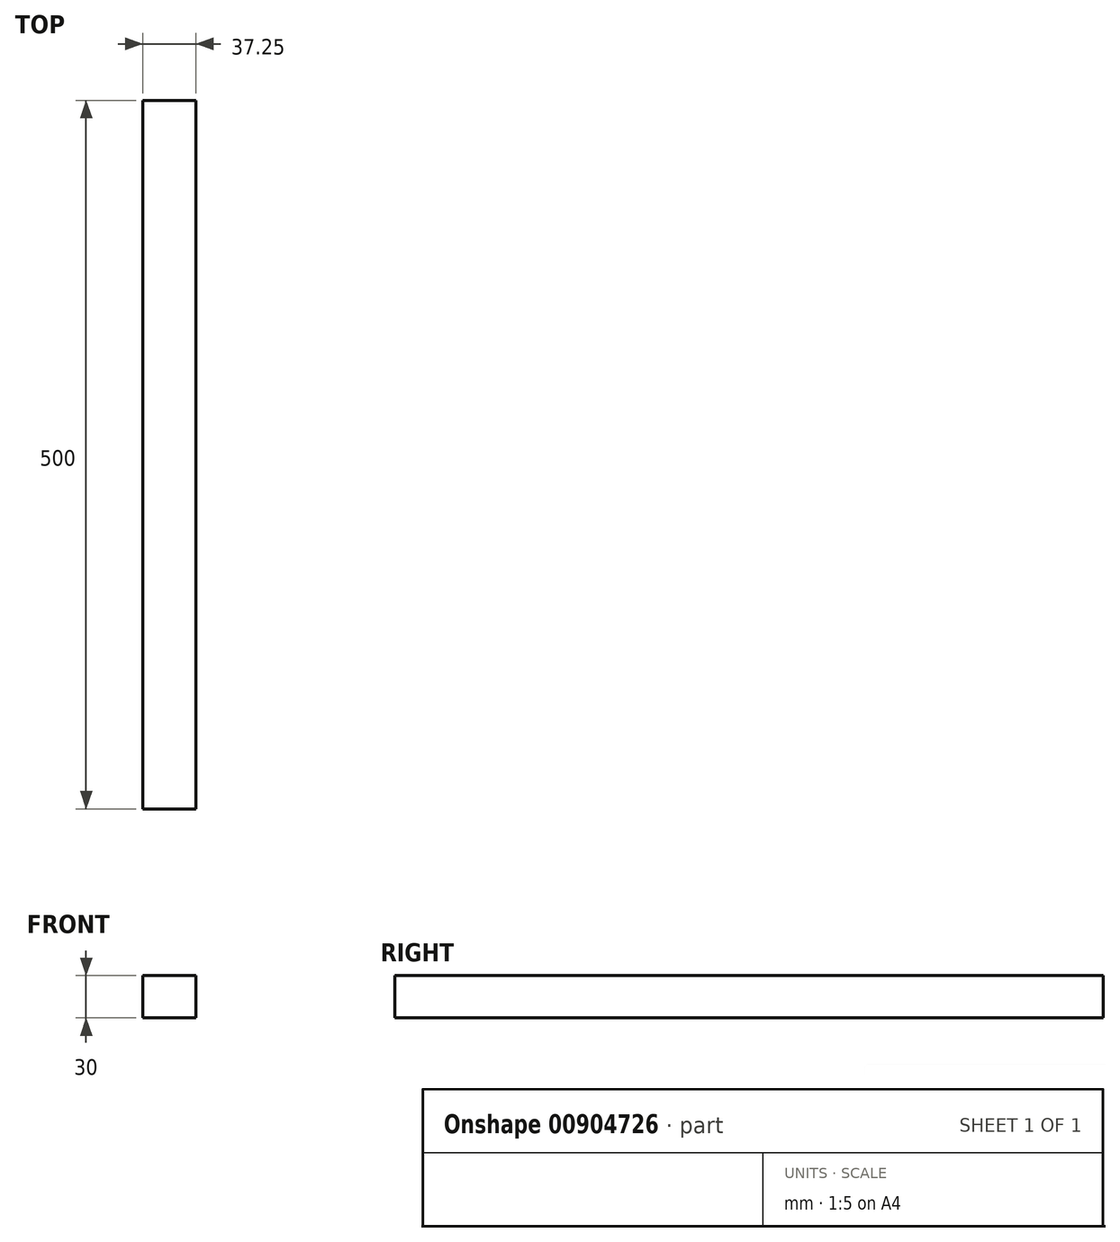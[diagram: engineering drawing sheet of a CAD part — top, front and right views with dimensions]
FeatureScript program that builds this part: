
annotation { "Feature Type Name" : "Feature", "Feature Type Description" : "" }
export const myFeature = defineFeature(function(context is Context, id is Id, definition is map)
    precondition{}
    {
        {
            var Q0;
            Q0=qCreatedBy(makeId("Front.planeOp"),FACE);
            var sketch = newSketch(context, id + "F0", { "sketchPlane" : qUnion([Q0])});
            skLineSegment(sketch, "E0.bottom", {"start": v(0, 0) * mm, "end": v(37.25, 0) * mm});
            skLineSegment(sketch, "E0.top", {"start": v(0, 30) * mm, "end": v(37.25, 30) * mm});
            skLineSegment(sketch, "E0.left", {"start": v(0, 0) * mm, "end": v(0, 30) * mm});
            skLineSegment(sketch, "E0.right", {"start": v(37.25, 0) * mm, "end": v(37.25, 30) * mm});
            skSolve(sketch);
        }
        {
            var Q0;
            Q0=makeQuery(id+"F0.imprint","IMPRINT",FACE,{"disambiguationData":[TD([[makeQuery(id+"F0.imprint","IMPRINT",EDGE,{"derivedFrom":sQuery(id+"F0.wireOp",EDGE,"E0.bottom")}),1.0]])]});
            extrude(context, id + "F1", {"entities" : qUnion([Q0]), "depth" : 500 * mm, "offsetDistance" : 25 * mm});
        }
    });
